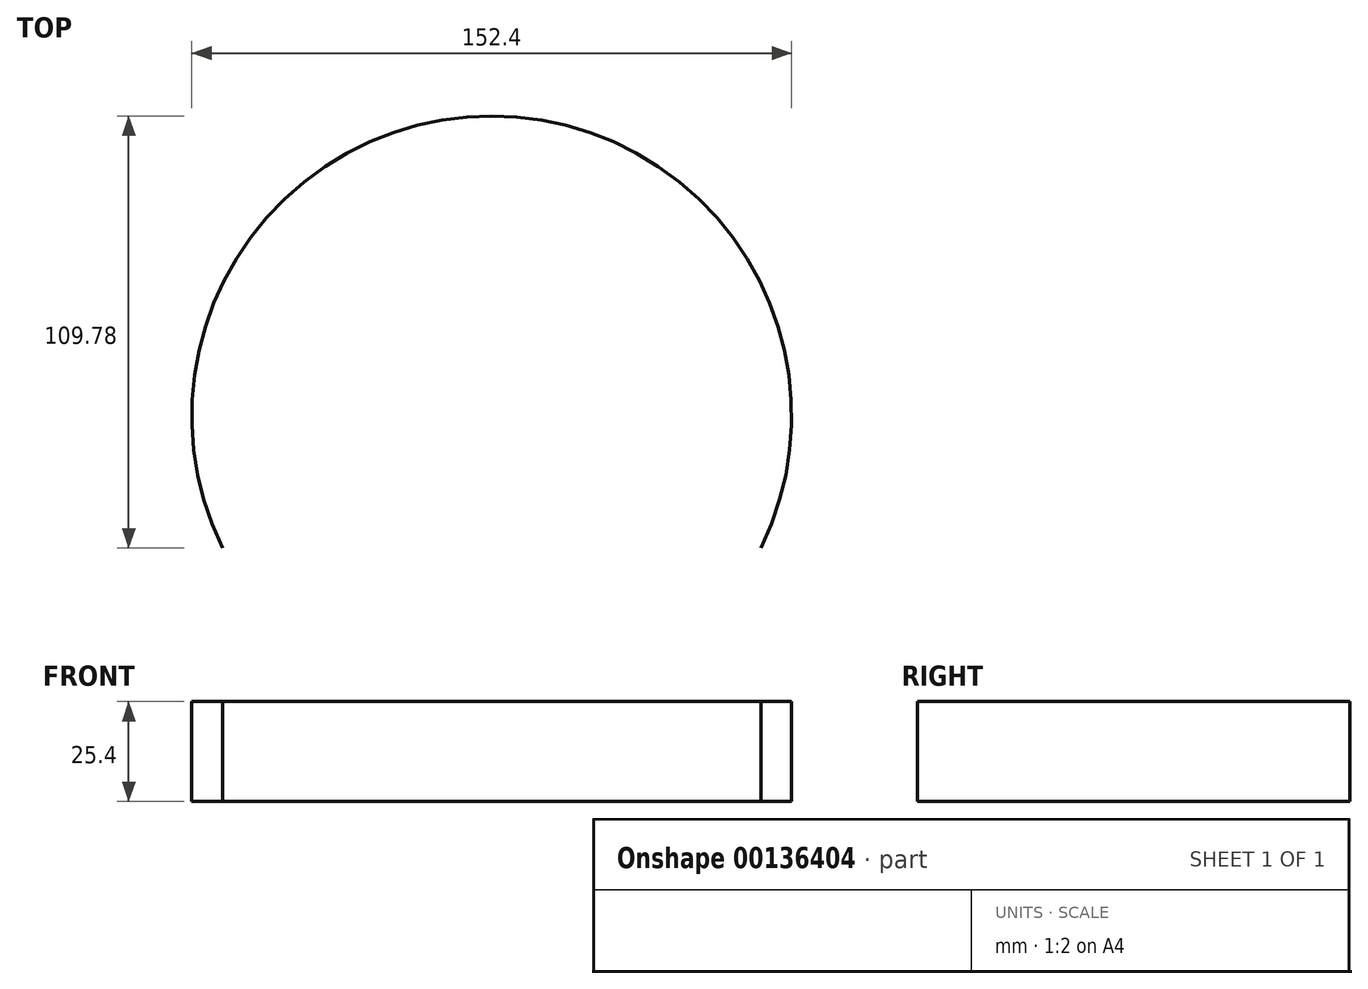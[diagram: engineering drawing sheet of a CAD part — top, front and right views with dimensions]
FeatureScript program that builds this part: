
annotation { "Feature Type Name" : "Feature", "Feature Type Description" : "" }
export const myFeature = defineFeature(function(context is Context, id is Id, definition is map)
    precondition{}
    {
        {
            var Q0;
            Q0=qCreatedBy(makeId("Top.planeOp"),FACE);
            var sketch = newSketch(context, id + "F0", { "sketchPlane" : qUnion([Q0])});
            skArc(sketch, "E0", {"start": v(70.8, 0) * mm, "mid": v(2.4, 109.78) * mm, "end": v(-66, 0) * mm});
            skSolve(sketch);
        }
        {
            var Q0;
            Q0=sQuery(id+"F0.wireOp",EDGE,"E0");
            extrude(context, id + "F1", {"bodyType" : ToolBodyType.SURFACE, "surfaceEntities" : qUnion([Q0]), "depth" : 25.4 * mm});
        }
    });
